# Revit family: ed
name_source: partatom
category: Generic Models
revit_build: Autodesk Revit 2018 (Build: 20190510_1515(x64)
units: mm (PartAtom-declared; Revit-internal decimal feet)

## family parameters
Always vertical = No
Can host rebar = No
Cut with Voids When Loaded = No
OmniClass Number = 23.19.31.17
OmniClass Title = Sanitary Room Units
Part Type = Normal
Room Calculation Point = No
Round Connector Dimension = Use Diameter
Shared = No
Work Plane-Based = Yes

## types (2) — shared parameters
BIMobject category = Bathroom Accessories
BIMobject category code = sanitary-accessories1
BIMobject main category = Sanitary
BIMobject main category code = sanitary
Brand url = http://www.duravit.com
Default Elevation = 1219.2 mm  [stored 4 ft]
Design country = Germany
ETIM classification = EC010555 | Lavatory brush set
Edition number = 1
IFC Classification = Furnishing Element
Installation instructions = https://pro.duravit.com
Manufacturer = Duravit
Manufacturer country = Germany
Manufacturer name = DURAVIT AG
Masterformat 2014 Code = 01 52 19
Masterformat 2014 Description = Sanitary Facilities
Material main = Brass
Material secondary = Plastic
Model = Starck T Brush set 80x80x432 mm - 009945
OmniClass Code = 23-19 31 17
OmniClass Description = Sanitary Room Units
Product Guid = 534bacf1-1e6d-4bcf-88f7-75a50d980427
Product SKU = Starck-T-Brush-set-80x80x432-mm-009945
Product certification = https://pro.duravit.com
Product data url = https://bimobject.com
Product family = Starck T
Product group = Brush set
Product name = Starck T Brush set 80x80x432 mm - 009945
Product url = https://pro.duravit.com
QR code = https://bimobject.com
Technical description = https://pro.duravit.com
UNSPSC Code = 301815
URL = https://www.duravit.com
Uniclass 2015 Code = Pr_40_20
Uniclass 2015 Name = Sanitary fittings and accessories
Uniformat II Code = D2010
Uniformat II Description = Plumbing Fixtures
Weight Net (Kg) = 1.22
Youtube clip = https://pro.duravit.com

## per-type parameters (varying)
| type | Description | Main material |
| 10 - Chrome | Duravit Starck T Brush set Chrome 80x80x432 mm - 0099451000 | Duravit - Metal - 10 - Chrome |
| 46 -  Black Matt | Duravit Starck T Brush set Black Matt 80x80x432 mm - 0099454600 | Duravit - Metal - 46 - Black Matt |

note: [stored X ft] marks values corroborated as IEEE doubles in the binary element streams (Revit-internal decimal feet)

## geometry (parser evidence)
native form markers: Sweep x4
no freeform markers — native parametric forms only
